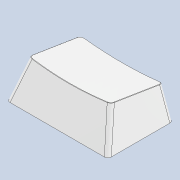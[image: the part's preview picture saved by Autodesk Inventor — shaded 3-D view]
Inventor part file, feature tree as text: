
AUTODESK INVENTOR PART (.ipt)
format: ipt  version: 2021 (Build 250183000, 183)  size: 243,712 bytes
history: native  units: in
note: dims shown in document units (in); Inventor stores cm internally (conversion verified against a paired STEP export)
features: chamfer x1
ambient origin geometry x8: Origin, YZ Plane, XZ Plane, XY Plane, X Axis, Y Axis, Z Axis, Center Point
bodies: Solid1 (feature_tree)
feature tree (1):
  chamfer  "Chamfer1"  [1 undecoded]
note: 1 required parameter value undecoded (feature->parameter linkage not recoverable at this tier; creation-order binding heuristic only, values carry confidence <= 0.55)
